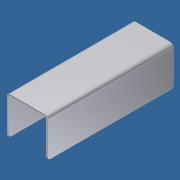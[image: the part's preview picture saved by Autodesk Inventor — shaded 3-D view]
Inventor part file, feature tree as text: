
AUTODESK INVENTOR PART (.ipt)
format: ipt  version: 2012 (Build 160160000, 160)  size: 90,112 bytes
history: native  units: in
note: dims shown in document units (in); Inventor stores cm internally (conversion verified against a paired STEP export)
features: other x3, sketch x1
ambient origin geometry x8: Origin, YZ Plane, XZ Plane, XY Plane, X Axis, Y Axis, Z Axis, Center Point
bodies: Solid1 (feature_tree)
feature tree (4):
  other  "GE-12052.ipt"
  other  "Solid1::GE-12052.ipt"
  sketch  "Sketch1"  dims[d0=0.3937in]
  other  "TaggingFeature1"
